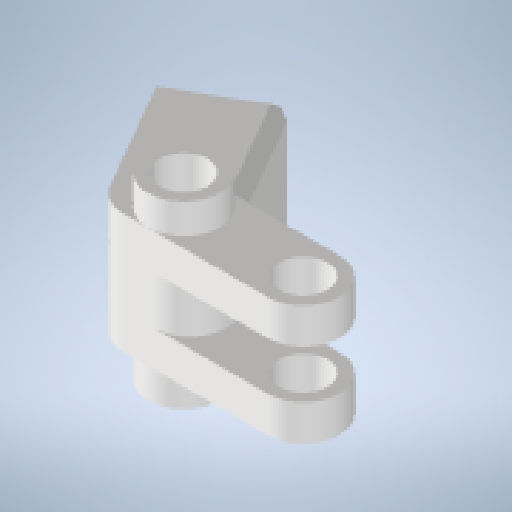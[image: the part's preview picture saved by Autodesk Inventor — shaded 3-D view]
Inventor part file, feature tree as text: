
AUTODESK INVENTOR PART (.ipt)
format: ipt  version: 2023.2 (Build 272271030, 271C)  size: 395,776 bytes
history: native  units: mm
features: sketch x6, chamfer x6, extrude x5, plane x1, mirror x1, hole x1, thread x1
ambient origin geometry x8: Origin, YZ Plane, XZ Plane, XY Plane, X Axis, Y Axis, Z Axis, Center Point
bodies: Solid1 (feature_tree)
feature tree (21):
  extrude  "Extrusion1"  Depth=6.0mm
  sketch  "Sketch2"  dims[d4=8.0mm d5=8.0mm]
  plane  "Work Plane1"
  mirror  "Mirror1"
  extrude  "Extrusion2"  Depth=8.0mm
  chamfer  "Chamfer1"  Distance=12.0mm
  chamfer  "Chamfer2"  Distance=20.0mm
  chamfer  "Chamfer3"  Distance=6.0mm
  chamfer  "Chamfer4"  Distance=25.0mm
  chamfer  "Chamfer5"  Distance=6.0mm
  chamfer  "Chamfer6"  Distance=12.0mm
  extrude  "Extrusion3"  Depth=3.0mm
  extrude  "Extrusion4"  Depth=12.0mm
  extrude  "Extrusion5"  Depth=8.0mm
  hole  "Hole2"  [1 undecoded]
  thread  "Thread1"  [1 undecoded]
  sketch  "Sketch1"  dims[d1=12.0mm d2=6.0mm]
  sketch  "Sketch3"  dims[d9=12.0mm]
  sketch  "Sketch5"  dims[d14=60.0deg]
  sketch  "Sketch6"  dims[d15=16.0mm]
  sketch  "Sketch7"  dims[d16=120.0deg d17=12.0mm d21=20.0mm d22=6.0mm d23=25.0mm d24=6.0mm d25=0.0mm d26=12.0mm d27=3.0mm d28=12.0mm d30=8.0mm d32=6.0mm d33=4.0mm d34=8.0mm d35=0.0mm d36=2.0mm d37=2.0mm d38=45.0deg d39=2.0mm d40=2.0mm d41=45.0deg d42=2.0mm d43=2.0mm d44=45.0deg d45=2.0mm d46=2.0mm d47=45.0deg d48=2.0mm d49=2.0mm d50=45.0deg d51=2.0mm d52=2.0mm d53=45.0deg d54=12.0mm d55=0.01mm d56=0.0mm d66=8.0mm d68=12.0mm d69=5.0mm d70=0.0mm d73=8.0mm d75=12.0mm d76=5.0mm d77=0.0mm d78=12.0mm d79=12.0mm d80=6.0mm d81=4.0mm d82=2.0mm d83=90.0deg d84=16.0mm d85=20.594885mm d86=16.0mm d87=0.0mm d57=1.0mm d58=1.0mm d59=1.0mm d60=0.15mm d61=0.25mm d62=0.375mm d63=14.3117mm d64=0.75mm d65=20.594885mm d67=0.75mm]
note: 2 required parameter values undecoded (feature->parameter linkage not recoverable at this tier; creation-order binding heuristic only, values carry confidence <= 0.55)
